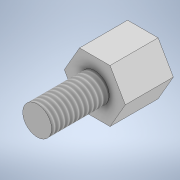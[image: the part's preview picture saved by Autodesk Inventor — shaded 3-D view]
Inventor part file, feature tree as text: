
AUTODESK INVENTOR PART (.ipt)
format: ipt  version: 2020 (Build 240168000, 168)  size: 117,248 bytes
history: native  units: mm
features: extrude x3, sketch x3, thread x2
ambient origin geometry x8: Origin, YZ Plane, XZ Plane, XY Plane, X Axis, Y Axis, Z Axis, Center Point
bodies: Solid1 (feature_tree)
feature tree (8):
  extrude  "Extrusion1"  Depth=5.0mm TaperAngle=0.0deg
  extrude  "Extrusion2"  Depth=6.0mm TaperAngle=0.0deg
  thread  "Thread1"  [1 undecoded]
  extrude  "Extrusion3"  Depth=5.0mm TaperAngle=0.0deg
  thread  "Thread2"  [1 undecoded]
  sketch  "Sketch1"  dims[d0=2.75mm d1=5.0mm d2=0.0mm]
  sketch  "Sketch2"  dims[d3=3.0mm d4=6.0mm d5=0.0mm d6=6.0mm d7=0.0mm]
  sketch  "Sketch3"  dims[d8=3.0mm d9=5.0mm d10=0.0mm d11=5.0mm d12=0.0mm]
note: 2 required parameter values undecoded (feature->parameter linkage not recoverable at this tier; creation-order binding heuristic only, values carry confidence <= 0.55)
